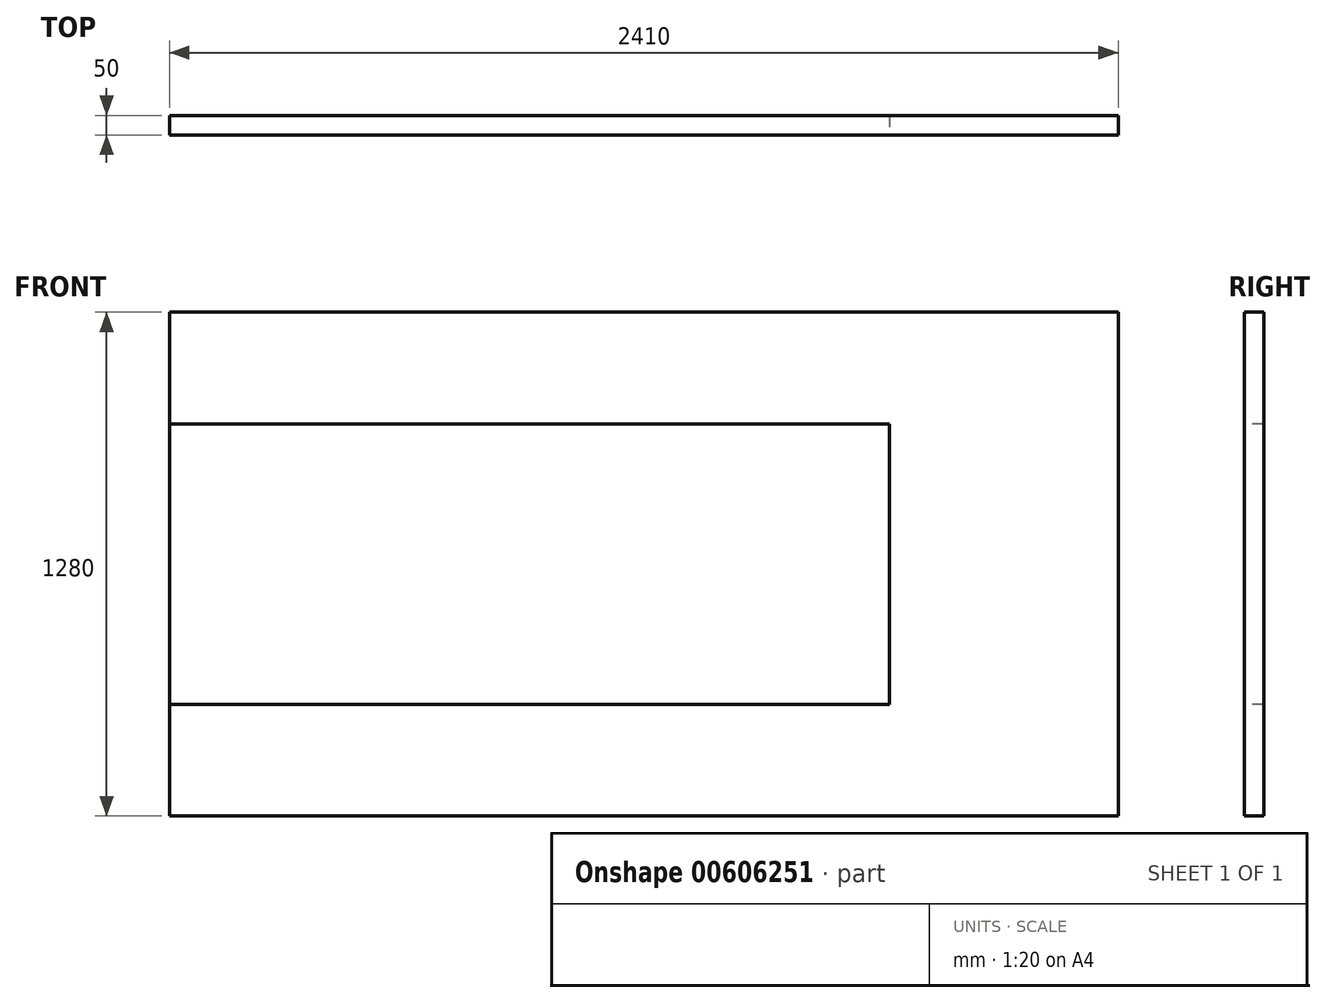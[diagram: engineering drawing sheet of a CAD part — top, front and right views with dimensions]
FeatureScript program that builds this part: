
annotation { "Feature Type Name" : "Feature", "Feature Type Description" : "" }
export const myFeature = defineFeature(function(context is Context, id is Id, definition is map)
    precondition{}
    {
        {
            var Q0;
            Q0=qCreatedBy(makeId("Front.planeOp"),FACE);
            var sketch = newSketch(context, id + "F0", { "sketchPlane" : qUnion([Q0])});
            skLineSegment(sketch, "E0.bottom", {"start": v(-1196.8, 573.64) * mm, "end": v(1213.2, 573.64) * mm});
            skLineSegment(sketch, "E0.top", {"start": v(-1196.8, -706.36) * mm, "end": v(1213.2, -706.36) * mm});
            skLineSegment(sketch, "E0.left", {"start": v(-1196.8, 573.64) * mm, "end": v(-1196.8, -706.36) * mm});
            skLineSegment(sketch, "E0.right", {"start": v(1213.2, 573.64) * mm, "end": v(1213.2, -706.36) * mm});
            skSolve(sketch);
        }
        {
            var Q0;
            Q0=qSketchRegion(id+"F0",true);
            extrude(context, id + "F1", {"entities" : qUnion([Q0]), "depth" : 50 * mm, "offsetDistance" : 25 * mm});
        }
        {
            var Q0;
            Q0=makeQuery(id+"F1.opExtrude","CAP_FACE",FACE,{"disambiguationData":[OSD([sQuery(id+"F0.wireOp",EDGE,"E0.bottom"),sQuery(id+"F0.wireOp",EDGE,"E0.top"),sQuery(id+"F0.wireOp",EDGE,"E0.left"),sQuery(id+"F0.wireOp",EDGE,"E0.right")])],"isStart":false});
            var sketch = newSketch(context, id + "F2", { "sketchPlane" : qUnion([Q0])});
            skLineSegment(sketch, "E1.bottom", {"start": v(-1196.8, 289.64) * mm, "end": v(632.2, 289.64) * mm});
            skLineSegment(sketch, "E1.top", {"start": v(-1196.8, -422.36) * mm, "end": v(632.2, -422.36) * mm});
            skLineSegment(sketch, "E1.left", {"start": v(-1196.8, 289.64) * mm, "end": v(-1196.8, -422.36) * mm});
            skLineSegment(sketch, "E1.right", {"start": v(632.2, 289.64) * mm, "end": v(632.2, -422.36) * mm});
            skSolve(sketch);
        }
        {
            var Q0;
            Q0=qSketchRegion(id+"F2",true);
            extrude(context, id + "F3", {"entities" : qUnion([Q0]), "oppositeDirection" : true, "depth" : 50 * mm, "offsetDistance" : 25 * mm});
        }
    });
